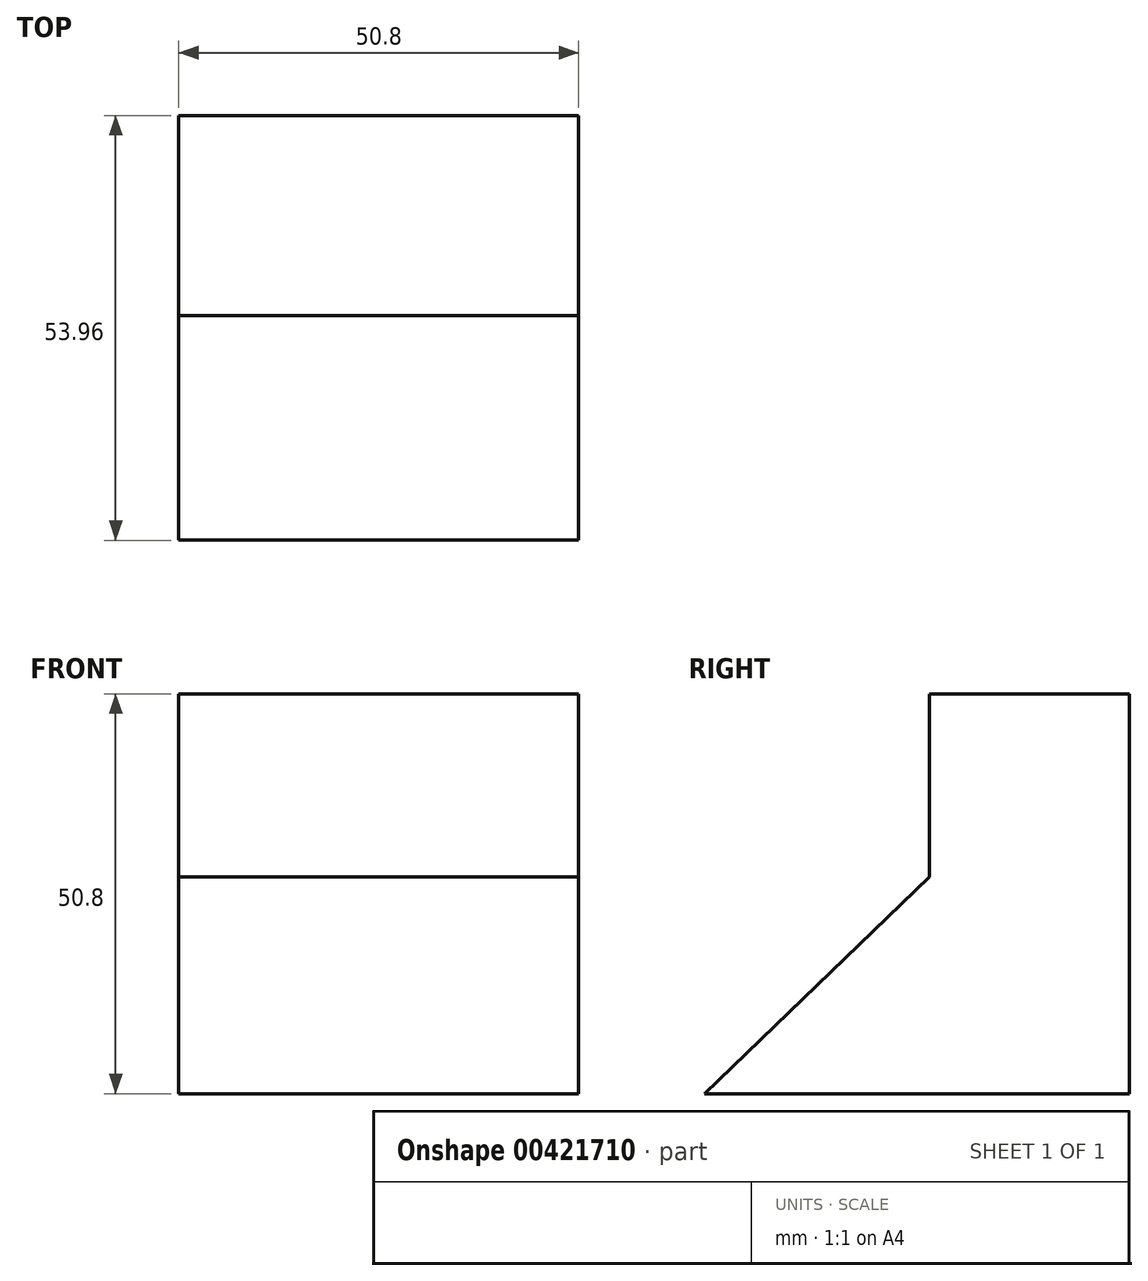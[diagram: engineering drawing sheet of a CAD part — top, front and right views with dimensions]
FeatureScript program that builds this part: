
annotation { "Feature Type Name" : "Feature", "Feature Type Description" : "" }
export const myFeature = defineFeature(function(context is Context, id is Id, definition is map)
    precondition{}
    {
        {
            var Q0;
            Q0=qCreatedBy(makeId("Front.planeOp"),FACE);
            var sketch = newSketch(context, id + "F0", { "sketchPlane" : qUnion([Q0])});
            skLineSegment(sketch, "E0.bottom", {"start": v(0, 0) * mm, "end": v(50.8, 0) * mm});
            skLineSegment(sketch, "E0.top", {"start": v(0, 50.8) * mm, "end": v(50.8, 50.8) * mm});
            skLineSegment(sketch, "E0.left", {"start": v(0, 0) * mm, "end": v(0, 50.8) * mm});
            skLineSegment(sketch, "E0.right", {"start": v(50.8, 0) * mm, "end": v(50.8, 50.8) * mm});
            skSolve(sketch);
        }
        {
            var Q0;
            Q0=makeQuery(id+"F0.imprint","IMPRINT",FACE,{"disambiguationData":[TD([[makeQuery(id+"F0.imprint","IMPRINT",EDGE,{"derivedFrom":sQuery(id+"F0.wireOp",EDGE,"E0.bottom")}),1.0]])]});
            extrude(context, id + "F1", {"entities" : qUnion([Q0]), "depth" : 25.4 * mm});
        }
        {
            var Q0;
            Q0=makeQuery(id+"F1.opExtrude","SWEPT_FACE",FACE,{"disambiguationData":[OSD([sQuery(id+"F0.wireOp",EDGE,"E0.right")])]});
            var sketch = newSketch(context, id + "F2", { "sketchPlane" : qUnion([Q0])});
            skLineSegment(sketch, "E1", {"start": v(-25.4, 27.52) * mm, "end": v(-53.96, 0) * mm});
            skLineSegment(sketch, "E2", {"start": v(-53.96, 0) * mm, "end": v(-25.4, 0) * mm});
            skLineSegment(sketch, "E3", {"start": v(-25.4, 0) * mm, "end": v(-25.4, 27.52) * mm});
            skSolve(sketch);
        }
        {
            var Q0;
            Q0=makeQuery(id+"F2.imprint","IMPRINT",FACE,{"disambiguationData":[TD([[makeQuery(id+"F2.imprint","IMPRINT",EDGE,{"derivedFrom":sQuery(id+"F2.wireOp",EDGE,"E1")}),1.0]])]});
            extrude(context, id + "F3", {"entities" : qUnion([Q0]), "operationType" : NewBodyOperationType.ADD, "oppositeDirection" : true, "depth" : 50.8 * mm});
        }
    });
